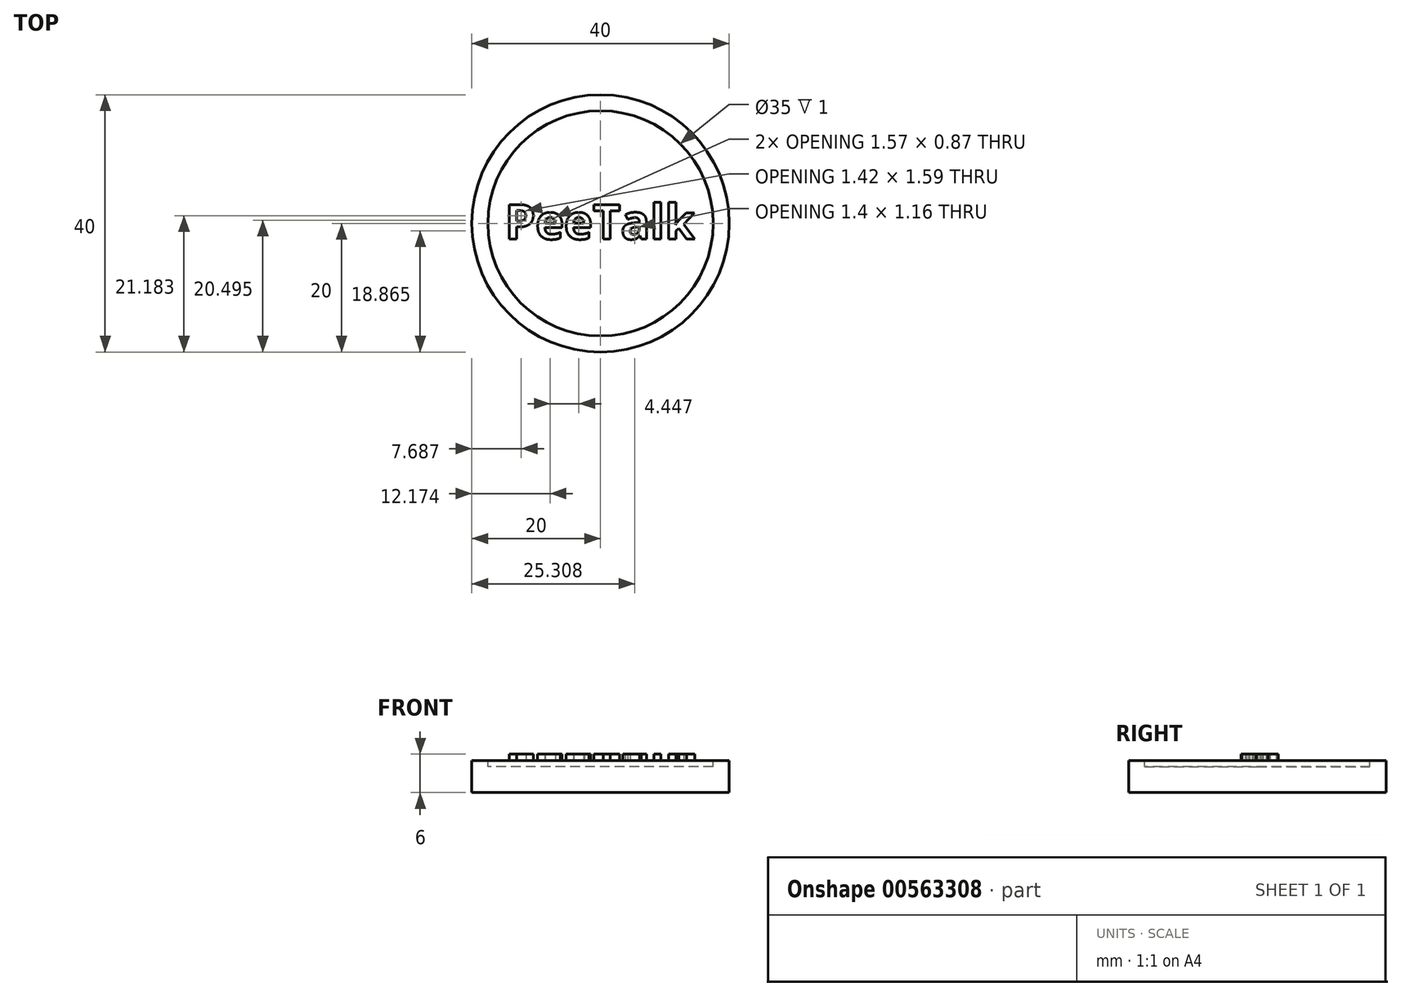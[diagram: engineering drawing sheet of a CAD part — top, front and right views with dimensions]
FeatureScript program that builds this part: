
annotation { "Feature Type Name" : "Feature", "Feature Type Description" : "" }
export const myFeature = defineFeature(function(context is Context, id is Id, definition is map)
    precondition{}
    {
        {
            var Q0;
            Q0=qCreatedBy(makeId("Top.planeOp"),FACE);
            var sketch = newSketch(context, id + "F0", { "sketchPlane" : qUnion([Q0])});
            skCircle(sketch, "E0", {"center": v(0, 0) * mm, "radius": 20 * mm});
            skSolve(sketch);
        }
        {
            var Q0;
            Q0=makeQuery(id+"F0.imprint","IMPRINT",FACE,{"disambiguationData":[TD([[makeQuery(id+"F0.imprint","IMPRINT",EDGE,{"derivedFrom":sQuery(id+"F0.wireOp",EDGE,"E0")}),1.0]])]});
            extrude(context, id + "F1", {"entities" : qUnion([Q0]), "depth" : 5 * mm, "offsetDistance" : 25.4 * mm});
        }
        {
            var Q0;
            Q0=makeQuery(id+"F1.opExtrude","CAP_FACE",FACE,{"disambiguationData":[OSD([sQuery(id+"F0.wireOp",EDGE,"E0")])],"isStart":false});
            var sketch = newSketch(context, id + "F2", { "sketchPlane" : qUnion([Q0])});
            skCircle(sketch, "E1", {"center": v(0, 0) * mm, "radius": 17.5 * mm});
            skSolve(sketch);
        }
        {
            var Q0;
            Q0=makeQuery(id+"F2.imprint","IMPRINT",FACE,{"disambiguationData":[TD([[makeQuery(id+"F2.imprint","IMPRINT",EDGE,{"derivedFrom":sQuery(id+"F2.wireOp",EDGE,"E1")}),1.0]])]});
            extrude(context, id + "F3", {"entities" : qUnion([Q0]), "operationType" : NewBodyOperationType.REMOVE, "oppositeDirection" : true, "depth" : 1 * mm, "offsetDistance" : 25.4 * mm});
        }
        {
            var Q0;
            Q0=makeQuery(id+"F2.imprint","IMPRINT",FACE,{"disambiguationData":[TD([[makeQuery(id+"F2.imprint","IMPRINT",EDGE,{"derivedFrom":sQuery(id+"F2.wireOp",EDGE,"E1")}),1.0]])]});
            var sketch = newSketch(context, id + "F4", { "sketchPlane" : qUnion([Q0])});
            skText(sketch, "E2", { "text": "PeeTalk", "fontName": "OpenSans-Bold.ttf"});
            const initialGuessF4  = {"E2": [-0.01484, -0.00246, 1, 0, 0.00542]};
            skSetInitialGuess(sketch, initialGuessF4);
            skSolve(sketch);
        }
        {
            var Q0;
            Q0 = qSketchRegion(id + "F4", true);
            extrude(context, id + "F5", {"entities" : qUnion([Q0]), "operationType" : NewBodyOperationType.ADD, "depth" : 1 * mm, "offsetDistance" : 25 * mm});
        }
    });
